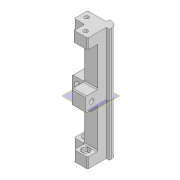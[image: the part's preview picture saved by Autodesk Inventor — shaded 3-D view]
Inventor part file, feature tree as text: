
AUTODESK INVENTOR PART (.ipt)
format: ipt  version: 2020 (Build 240168000, 168)  size: 329,728 bytes
history: native  units: mm
features: extrude x12, sketch x12, other x6, fillet x2
ambient origin geometry x8: Origin, YZ Plane, XZ Plane, XY Plane, X Axis, Y Axis, Z Axis, Center Point
bodies: Body1 (feature_tree)
feature tree (32):
  other  "Sólido1"
  extrude  "Extrusão1"  Depth=16.0mm
  extrude  "Extrusão2"  Depth=3.0mm
  extrude  "Extrusão3"  Depth=3.0mm
  extrude  "Extrusão4"  Depth=5.2mm
  extrude  "Extrusão5"  Depth=8.0mm
  fillet  "Arredondamento1"  Radius=110.0mm
  extrude  "Extrusão6"  Depth=10.0mm
  extrude  "Extrusão7"  TaperAngle=0.0deg  [1 undecoded]
  other  "Plano de trabalho1"
  extrude  "Extrusão9"  Depth=5.0mm
  extrude  "Extrusão10"  Depth=10.0mm
  extrude  "Extrusão11"  Depth=4.0mm
  extrude  "Extrusão12"  Depth=5.0mm
  extrude  "Extrusão13"  Depth=1.0mm TaperAngle=0.0deg
  fillet  "Arredondamento2"  Radius=1.0mm
  sketch  "Esboço1"  dims[d0=16.0mm d1=16.0mm]
  sketch  "Esboço2"  dims[d2=8.0mm d3=3.0mm]
  sketch  "Esboço3"  dims[d4=8.0mm d5=3.0mm]
  sketch  "Esboço4"  dims[d6=6.0mm d7=5.2mm]
  sketch  "Esboço5"  dims[d8=8.0mm d9=8.0mm d10=110.0mm d11=0.0mm]
  sketch  "Esboço6"  dims[d12=10.0mm d13=10.0mm]
  sketch  "Esboço7"  dims[d14=10.0mm d15=0.0mm d16=0.0mm]
  other  "Contorno projetado1"
  other  "Contorno projetado2"
  sketch  "Esboço9"  dims[d17=4.0mm d18=5.0mm]
  other  "Contorno projetado3"
  other  "Contorno projetado4"
  sketch  "Esboço10"  dims[d19=200.0mm d20=0.0mm d21=10.0mm]
  sketch  "Esboço11"  dims[d22=10.0mm d23=0.0mm d24=4.0mm]
  sketch  "Esboço12"  dims[d25=5.0mm d26=7.0mm]
  sketch  "Esboço13"  dims[d27=6.0mm d28=200.0mm d29=0.0mm d30=1.0mm d31=13.0mm d32=6.95mm d33=6.95mm d34=4.0mm d35=0.0mm d36=4.0mm d37=0.0mm d38=0.0mm d44=0.0mm d45=-50.0mm d46=12.0mm d47=12.0mm d48=2.0mm d49=0.0mm d50=12.0mm d51=0.0mm d52=4.5mm d53=6.0mm d54=20.0mm d55=0.0mm d56=4.5mm d57=6.0mm d58=20.0mm d59=0.0mm d60=6.95mm d61=4.0mm d62=0.0mm d63=6.95mm d64=4.0mm d65=0.0mm d66=1.0mm]
note: 1 required parameter value undecoded (feature->parameter linkage not recoverable at this tier; creation-order binding heuristic only, values carry confidence <= 0.55)
